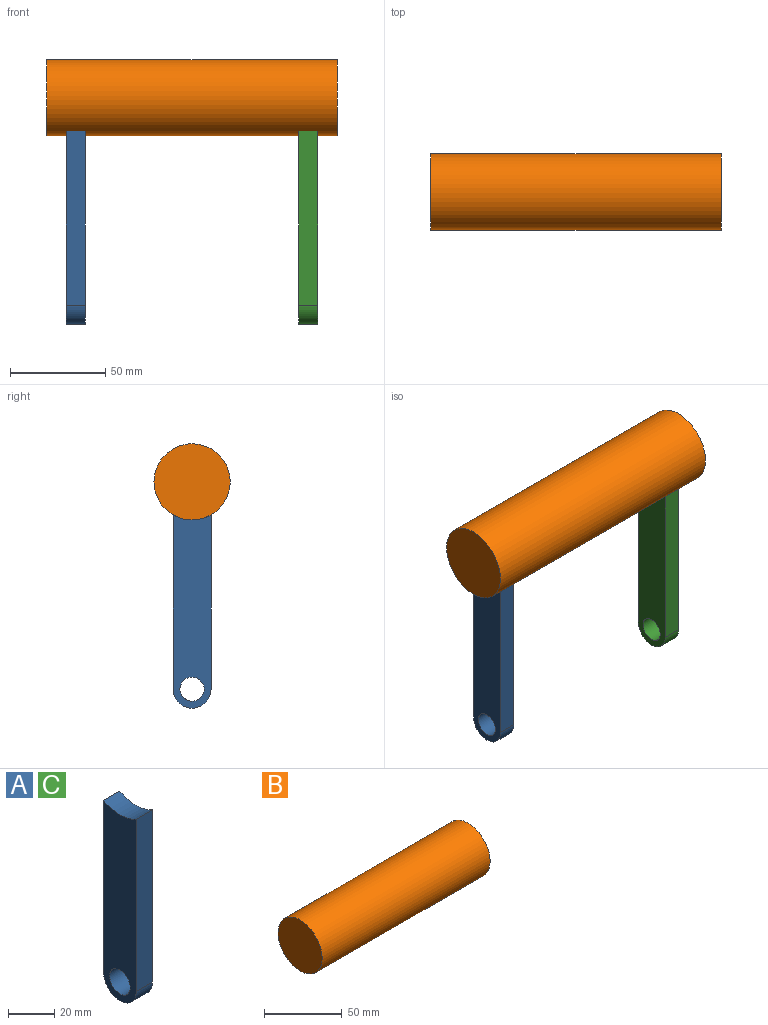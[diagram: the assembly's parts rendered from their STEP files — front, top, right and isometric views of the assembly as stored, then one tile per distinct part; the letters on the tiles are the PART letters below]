
ASSEMBLY  parts=3 mates=4
PART A: 7 faces, bbox 10x20x101.6 mm
  f0: plane 101.6x20mm, normal (-1,0,0), area 1826.2mm2, adj f1,f3,f4,f5,f6
  f1: plane 91.6x10mm, normal (0,-1,0), area 916mm2, adj f0,f2,f4,f6
  f2: plane 101.6x20mm, normal (1,0,0), area 1826.2mm2, adj f1,f3,f4,f5,f6
  f3: plane 91.6x10mm, normal (0,1,0), area 916mm2, adj f0,f2,f4,f6
  f4: cylinder r=20mm len=20mm, axis (-1,0,0), area 209.4mm2, adj f0,f1,f2,f3
  f5: cylinder r=6.35mm len=12.7mm, axis (-1,0,0), area 399mm2, adj f0,f2
  f6: cylinder r=10mm len=20mm, axis (-1,0,0), area 314.2mm2, adj f0,f1,f2,f3
PART B: 3 faces, bbox 152.4x40x40 mm
  f0: cylinder r=20mm len=152.4mm, axis (-1,0,0), area 19151.1mm2, adj f1,f2
  f1: plane 40x40mm, normal (1,0,0), area 1256.6mm2, adj f0
  f2: plane 40x40mm, normal (-1,0,0), area 1256.6mm2, adj f0
PART C: same geometry as A
PLACE A t=(-54.07,31.21,-29.49)mm
PLACE B t=(-64.07,21.21,89.43)mm
PLACE C t=(68.33,31.21,-29.49)mm
MATE planar A.f0 <-> B.f0  axis (-1,0,0) through (-54.07,21.21,24.29)mm
MATE cylindrical A.f4 <-> B.f0  axis (-1,0,0) through (-49.07,21.21,89.43)mm
MATE planar C.f2 <-> B.f0  axis (1,0,0) through (78.33,21.21,24.29)mm
MATE cylindrical B.f0 <-> C.f4  axis (-1,0,0) through (12.13,21.21,89.43)mm
